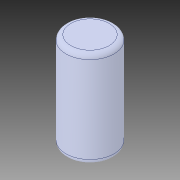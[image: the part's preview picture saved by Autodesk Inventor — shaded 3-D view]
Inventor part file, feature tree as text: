
AUTODESK INVENTOR PART (.ipt)
format: ipt  version: 2019 (Build 230136000, 136)  size: 107,520 bytes
history: native  units: in
note: dims shown in document units (in); Inventor stores cm internally (conversion verified against a paired STEP export)
features: fillet x1
ambient origin geometry x8: Origin, YZ Plane, XZ Plane, XY Plane, X Axis, Y Axis, Z Axis, Center Point
bodies: Solid1 (feature_tree)
feature tree (1):
  fillet  "Fillet1"  [1 undecoded]
note: 1 required parameter value undecoded (feature->parameter linkage not recoverable at this tier; creation-order binding heuristic only, values carry confidence <= 0.55)
